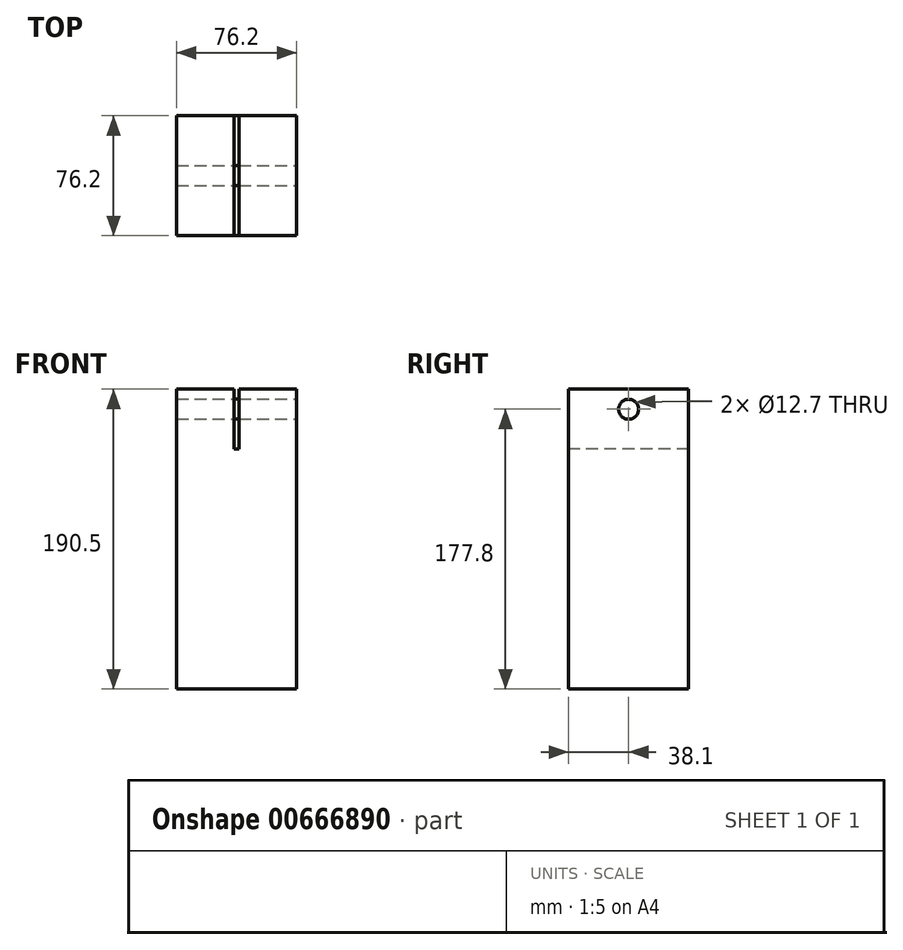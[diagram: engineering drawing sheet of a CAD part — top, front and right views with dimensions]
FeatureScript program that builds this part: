
annotation { "Feature Type Name" : "Feature", "Feature Type Description" : "" }
export const myFeature = defineFeature(function(context is Context, id is Id, definition is map)
    precondition{}
    {
        {
            var Q0;
            Q0=qCreatedBy(makeId("Top.planeOp"),FACE);
            var sketch = newSketch(context, id + "F0", { "sketchPlane" : qUnion([Q0])});
            skLineSegment(sketch, "E0.bottom", {"start": v(0, 0) * mm, "end": v(76.2, 0) * mm});
            skLineSegment(sketch, "E0.top", {"start": v(0, -76.2) * mm, "end": v(76.2, -76.2) * mm});
            skLineSegment(sketch, "E0.left", {"start": v(0, 0) * mm, "end": v(0, -76.2) * mm});
            skLineSegment(sketch, "E0.right", {"start": v(76.2, 0) * mm, "end": v(76.2, -76.2) * mm});
            skLineSegment(sketch, "E1", {"start": v(38.1, 0) * mm, "end": v(38.1, -76.2) * mm, "construction": true});
            skLineSegment(sketch, "E2", {"start": v(39.69, 0) * mm, "end": v(39.69, -76.2) * mm});
            skLineSegment(sketch, "E3.MirrorCS", {"start": v(36.51, 0) * mm, "end": v(36.51, -76.2) * mm});
            skSolve(sketch);
        }
        {
            var Q0;
            {var subQ0=sQuery(id+"F0.wireOp",EDGE,"E2");Q0=makeQuery(id+"F0.imprint","IMPRINT",FACE,{"disambiguationData":[TD([[makeQuery(id+"F0.imprint","IMPRINT",EDGE,{"derivedFrom":subQ0}),-1.0]])]});}
            var Q1;
            {var subQ0=sQuery(id+"F0.wireOp",EDGE,"E0.right");Q1=makeQuery(id+"F0.imprint","IMPRINT",FACE,{"disambiguationData":[TD([[makeQuery(id+"F0.imprint","IMPRINT",EDGE,{"derivedFrom":subQ0}),-1.0]])]});}
            var Q2;
            {var subQ0=sQuery(id+"F0.wireOp",EDGE,"E0.left");Q2=makeQuery(id+"F0.imprint","IMPRINT",FACE,{"disambiguationData":[TD([[makeQuery(id+"F0.imprint","IMPRINT",EDGE,{"derivedFrom":subQ0}),1.0]])]});}
            extrude(context, id + "F1", {"entities" : qUnion([Q0, Q1, Q2]), "oppositeDirection" : true, "depth" : 152.4 * mm, "offsetDistance" : 25.4 * mm});
        }
        {
            var Q0;
            {var subQ0=sQuery(id+"F0.wireOp",EDGE,"E0.left");Q0=makeQuery(id+"F0.imprint","IMPRINT",FACE,{"disambiguationData":[TD([[makeQuery(id+"F0.imprint","IMPRINT",EDGE,{"derivedFrom":subQ0}),1.0]])]});}
            var Q1;
            {var subQ0=sQuery(id+"F0.wireOp",EDGE,"E0.right");Q1=makeQuery(id+"F0.imprint","IMPRINT",FACE,{"disambiguationData":[TD([[makeQuery(id+"F0.imprint","IMPRINT",EDGE,{"derivedFrom":subQ0}),-1.0]])]});}
            extrude(context, id + "F2", {"entities" : qUnion([Q0, Q1]), "operationType" : NewBodyOperationType.ADD, "depth" : 38.1 * mm, "offsetDistance" : 25.4 * mm});
        }
        {
            var Q0;
            {var subQ0=sQuery(id+"F0.wireOp",EDGE,"E0.right");Q0=makeQuery(id+"F2.boolean.opBoolean","MERGE",FACE,{"derivedFrom":[makeQuery(id+"F1.opExtrude","SWEPT_FACE",FACE,{"disambiguationData":[OSD([subQ0])]}),makeQuery(id+"F2.opExtrude","SWEPT_FACE",FACE,{"disambiguationData":[OSD([subQ0])]})]});}
            var sketch = newSketch(context, id + "F3", { "sketchPlane" : qUnion([Q0])});
            skLineSegment(sketch, "E4", {"start": v(-38.1, 38.1) * mm, "end": v(-38.1, -36.35) * mm, "construction": true});
            skLineSegment(sketch, "E5", {"start": v(-76.2, 25.4) * mm, "end": v(0, 25.4) * mm, "construction": true});
            skCircle(sketch, "E6", {"center": v(-38.1, 25.4) * mm, "radius": 6.35 * mm});
            skSolve(sketch);
        }
        {
            var Q0;
            Q0=makeQuery(id+"F3.imprint","IMPRINT",FACE,{"disambiguationData":[TD([[makeQuery(id+"F3.imprint","IMPRINT",EDGE,{"derivedFrom":sQuery(id+"F3.wireOp",EDGE,"E6")}),1.0]])]});
            extrude(context, id + "F4", {"entities" : qUnion([Q0]), "operationType" : NewBodyOperationType.REMOVE, "endBound" : BoundingType.THROUGH_ALL, "oppositeDirection" : true, "depth" : 25.4 * mm, "offsetDistance" : 25.4 * mm});
        }
        {
            var Q0;
            {var subQ0=sQuery(id+"F0.wireOp",EDGE,"E0.right");Q0=makeQuery(id+"F2.boolean.opBoolean","MERGE",FACE,{"derivedFrom":[makeQuery(id+"F1.opExtrude","SWEPT_FACE",FACE,{"disambiguationData":[OSD([subQ0])]}),makeQuery(id+"F2.opExtrude","SWEPT_FACE",FACE,{"disambiguationData":[OSD([subQ0])]})]});}
            var sketch = newSketch(context, id + "F5", { "sketchPlane" : qUnion([Q0])});
            skCircle(sketch, "E7.0", {"center": v(-38.1, 25.4) * mm, "radius": 6.35 * mm});
            skSolve(sketch);
        }
        {
            var Q0;
            Q0=makeQuery(id+"F5.imprint","IMPRINT",FACE,{"disambiguationData":[TD([[makeQuery(id+"F5.imprint","IMPRINT",EDGE,{"derivedFrom":sQuery(id+"F5.wireOp",EDGE,"E7.0")}),1.0]])]});
            extrude(context, id + "F6", {"entities" : qUnion([Q0]), "oppositeDirection" : true, "depth" : 76.2 * mm, "offsetDistance" : 25.4 * mm});
        }
    });
